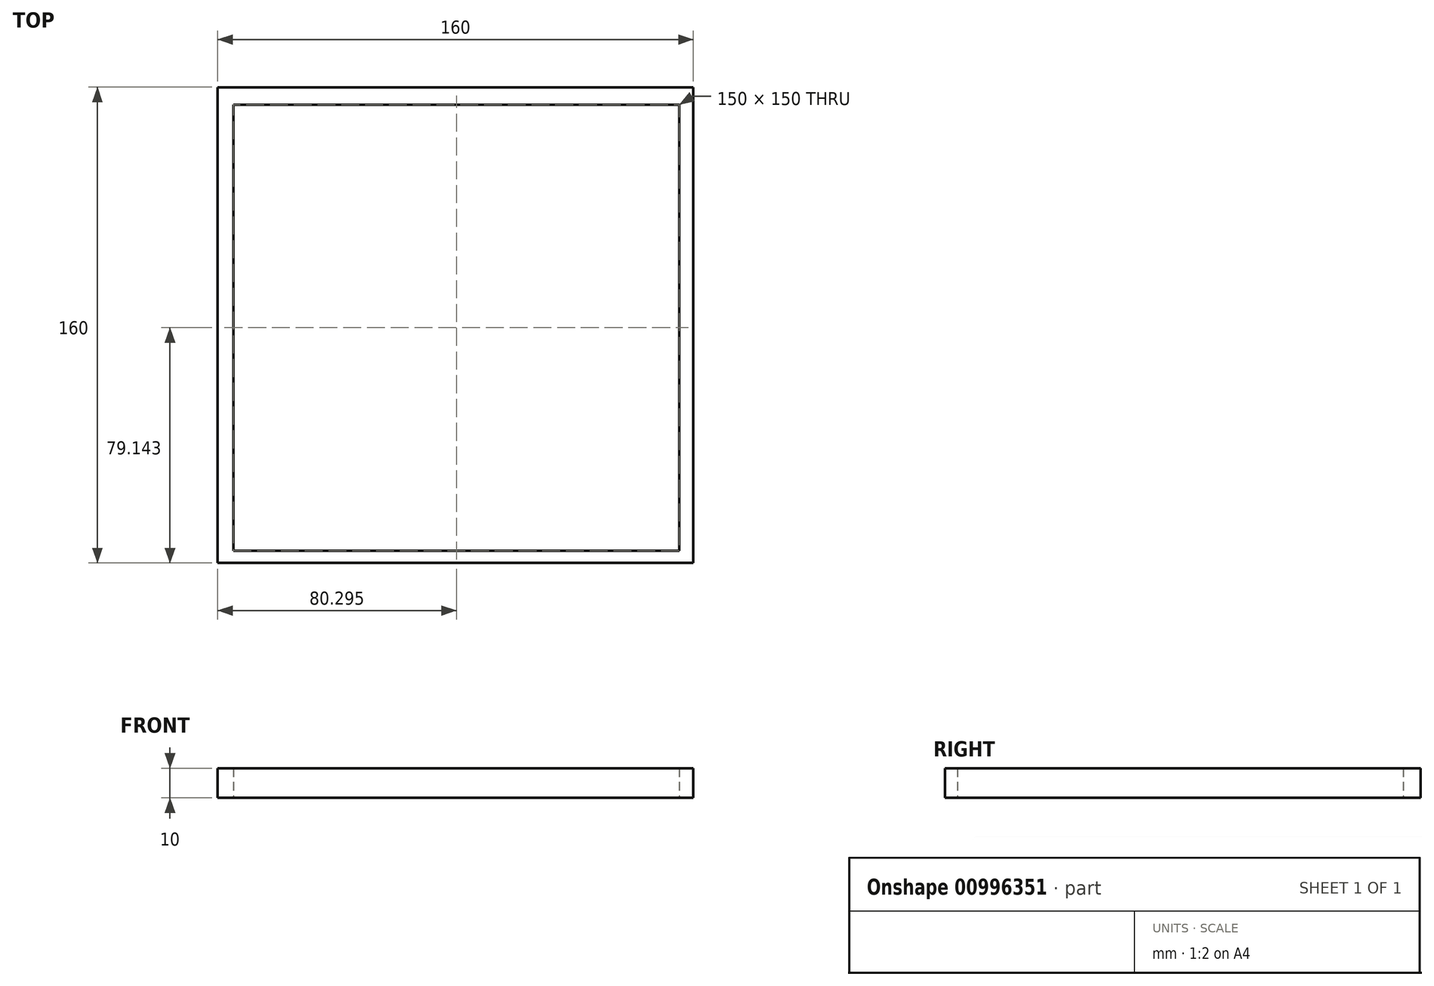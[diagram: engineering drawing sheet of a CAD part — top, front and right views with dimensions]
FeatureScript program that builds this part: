
annotation { "Feature Type Name" : "Feature", "Feature Type Description" : "" }
export const myFeature = defineFeature(function(context is Context, id is Id, definition is map)
    precondition{}
    {
        {
            var Q0;
            Q0=qCreatedBy(makeId("Top.planeOp"),FACE);
            var sketch = newSketch(context, id + "F0", { "sketchPlane" : qUnion([Q0])});
            skLineSegment(sketch, "E0.bottom", {"start": v(-66.9, 83.9) * mm, "end": v(93.1, 83.9) * mm});
            skLineSegment(sketch, "E0.top", {"start": v(-66.9, -76.1) * mm, "end": v(93.1, -76.1) * mm});
            skLineSegment(sketch, "E0.left", {"start": v(-66.9, 83.9) * mm, "end": v(-66.9, -76.1) * mm});
            skLineSegment(sketch, "E0.right", {"start": v(93.1, 83.9) * mm, "end": v(93.1, -76.1) * mm});
            skLineSegment(sketch, "E1.bottom", {"start": v(-61.6, 78.04) * mm, "end": v(88.4, 78.04) * mm});
            skLineSegment(sketch, "E1.top", {"start": v(-61.6, -71.96) * mm, "end": v(88.4, -71.96) * mm});
            skLineSegment(sketch, "E1.left", {"start": v(-61.6, 78.04) * mm, "end": v(-61.6, -71.96) * mm});
            skLineSegment(sketch, "E1.right", {"start": v(88.4, 78.04) * mm, "end": v(88.4, -71.96) * mm});
            skSolve(sketch);
        }
        {
            var Q0;
            Q0=makeQuery(id+"F0.imprint","IMPRINT",FACE,{"disambiguationData":[TD([[makeQuery(id+"F0.imprint","IMPRINT",EDGE,{"derivedFrom":sQuery(id+"F0.wireOp",EDGE,"E0.bottom")}),-1.0]])]});
            extrude(context, id + "F1", {"entities" : qUnion([Q0]), "depth" : 10 * mm, "offsetDistance" : 25 * mm});
        }
    });
